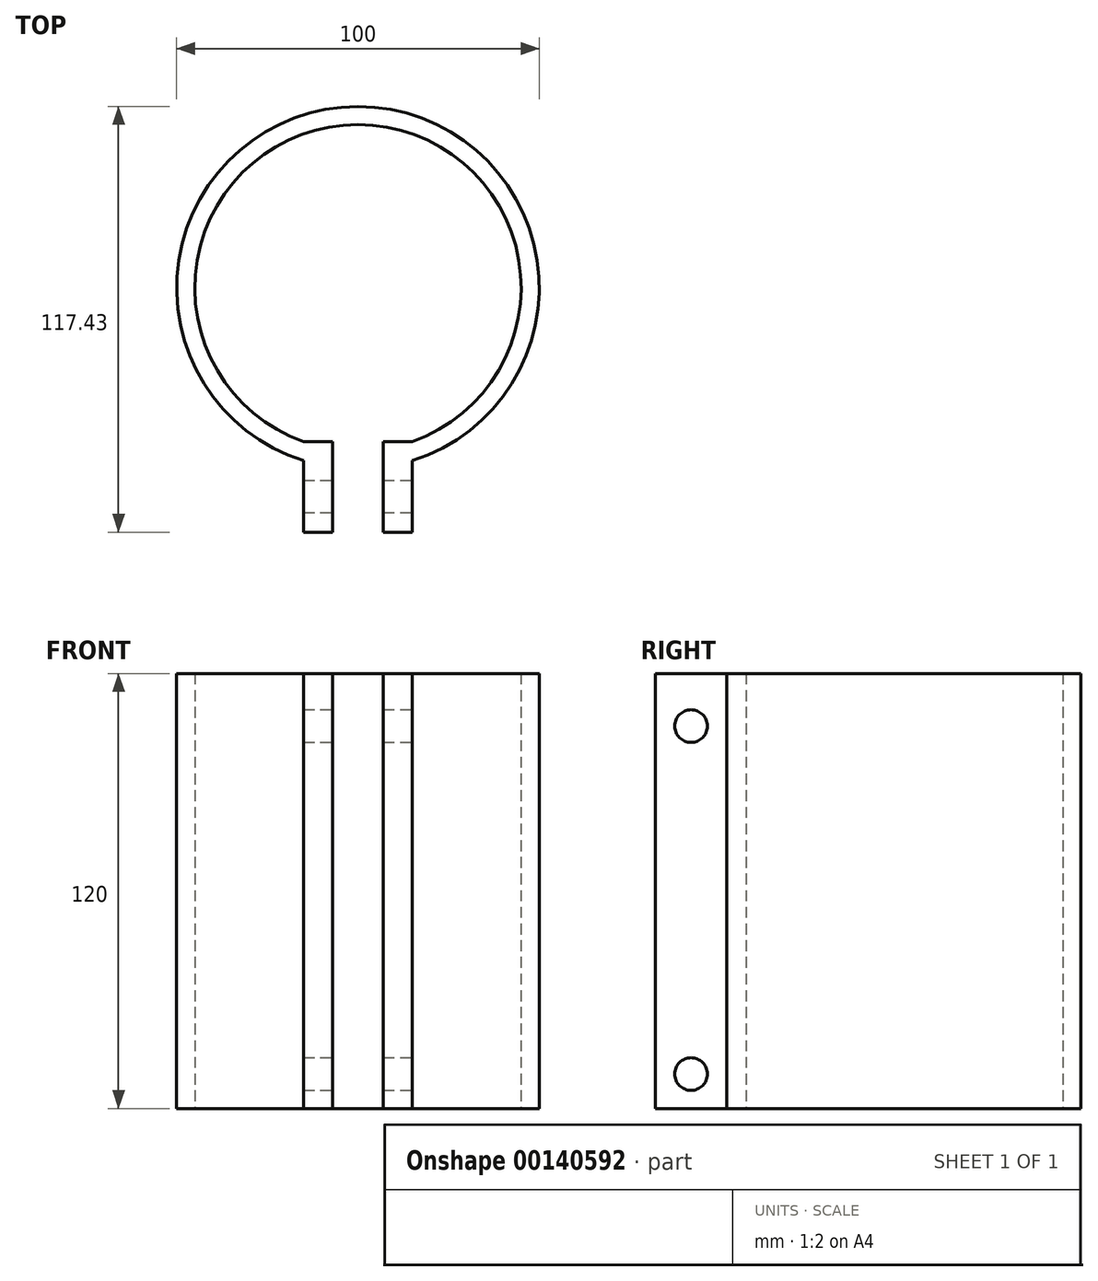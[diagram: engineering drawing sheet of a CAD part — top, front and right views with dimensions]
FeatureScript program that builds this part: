
annotation { "Feature Type Name" : "Feature", "Feature Type Description" : "" }
export const myFeature = defineFeature(function(context is Context, id is Id, definition is map)
    precondition{}
    {
        {
            var Q0;
            Q0=qCreatedBy(makeId("Top.planeOp"),FACE);
            var sketch = newSketch(context, id + "F0", { "sketchPlane" : qUnion([Q0])});
            skLineSegment(sketch, "E0", {"start": v(0, 56.78) * mm, "end": v(0, -71.57) * mm, "construction": true});
            skLineSegment(sketch, "E1", {"start": v(-72.55, 0) * mm, "end": v(74.1, 0) * mm, "construction": true});
            skPoint(sketch, "E2.middle", {"position": v(0, -50) * mm});
            skArc(sketch, "E3", {"start": v(15, -42.43) * mm, "mid": v(0, 45) * mm, "end": v(-15, -42.43) * mm});
            skArc(sketch, "E4", {"start": v(15, -47.7) * mm, "mid": v(0, 50) * mm, "end": v(-15, -47.7) * mm});
            skLineSegment(sketch, "E5.bottom", {"start": v(15, -42.43) * mm, "end": v(7, -42.43) * mm});
            skLineSegment(sketch, "E5.top", {"start": v(15, -67.43) * mm, "end": v(7, -67.43) * mm});
            skLineSegment(sketch, "E5.left", {"start": v(15, -42.43) * mm, "end": v(15, -67.43) * mm});
            skLineSegment(sketch, "E5.right", {"start": v(7, -42.43) * mm, "end": v(7, -67.43) * mm});
            skLineSegment(sketch, "E6.MirrorCS", {"start": v(-15, -42.43) * mm, "end": v(-7, -42.43) * mm});
            skLineSegment(sketch, "E7.MirrorCS", {"start": v(-7, -42.43) * mm, "end": v(-7, -67.43) * mm});
            skLineSegment(sketch, "E8.MirrorCS", {"start": v(-15, -42.43) * mm, "end": v(-15, -67.43) * mm});
            skLineSegment(sketch, "E9.MirrorCS", {"start": v(-15, -67.43) * mm, "end": v(-7, -67.43) * mm});
            skLineSegment(sketch, "E10", {"start": v(50, 0) * mm, "end": v(50, 78) * mm});
            skLineSegment(sketch, "E11", {"start": v(-50, 0) * mm, "end": v(-50, 78) * mm});
            skLineSegment(sketch, "E12", {"start": v(-48, 80) * mm, "end": v(48, 80) * mm});
            skPoint(sketch, "E13.visualSharp", {"position": v(-50, 80) * mm});
            skArc(sketch, "E13.filletArc", {"start": v(-48, 80) * mm, "mid": v(-49.41, 79.41) * mm, "end": v(-50, 78) * mm});
            skPoint(sketch, "E14.visualSharp", {"position": v(50, 80) * mm});
            skArc(sketch, "E14.filletArc", {"start": v(50, 78) * mm, "mid": v(49.41, 79.41) * mm, "end": v(48, 80) * mm});
            skArc(sketch, "E15.0", {"start": v(40, 44.72) * mm, "mid": v(0, 60) * mm, "end": v(-40, 44.72) * mm});
            skLineSegment(sketch, "E16.0", {"start": v(-40, 75) * mm, "end": v(40, 75) * mm});
            skLineSegment(sketch, "E17.trimOffspring", {"start": v(-40, 44.72) * mm, "end": v(-40, 75) * mm});
            skLineSegment(sketch, "E18.trimOffspring", {"start": v(40, 44.72) * mm, "end": v(40, 75) * mm});
            skLineSegment(sketch, "E19", {"start": v(-40, 75) * mm, "end": v(-50, 75) * mm});
            skLineSegment(sketch, "E20", {"start": v(40, 75) * mm, "end": v(50, 75) * mm});
            skSolve(sketch);
        }
        {
            var Q0;
            {var subQ7=sQuery(id+"F0.wireOp",EDGE,"E3");Q0=makeQuery(id+"F0.imprint","IMPRINT",FACE,{"disambiguationData":[TD([[makeQuery(id+"F0.imprint","IMPRINT",EDGE,{"derivedFrom":subQ7}),-1.0]])]});}
            var Q1;
            {var subQ3=sQuery(id+"F0.wireOp",EDGE,"E5.bottom");Q1=makeQuery(id+"F0.imprint","IMPRINT",FACE,{"disambiguationData":[TD([[makeQuery(id+"F0.imprint","IMPRINT",EDGE,{"derivedFrom":subQ3}),1.0]])]});}
            var Q2;
            {var subQ3=sQuery(id+"F0.wireOp",EDGE,"E6.MirrorCS");Q2=makeQuery(id+"F0.imprint","IMPRINT",FACE,{"disambiguationData":[TD([[makeQuery(id+"F0.imprint","IMPRINT",EDGE,{"derivedFrom":subQ3}),-1.0]])]});}
            extrude(context, id + "F1", {"entities" : qUnion([Q0, Q1, Q2]), "depth" : 120 * mm});
        }
        {
            var Q0;
            Q0=makeQuery(id+"F1.opExtrude","SWEPT_FACE",FACE,{"disambiguationData":[OSD([sQuery(id+"F0.wireOp",EDGE,"E5.left")])]});
            var sketch = newSketch(context, id + "F2", { "sketchPlane" : qUnion([Q0])});
            skCircle(sketch, "E21", {"center": v(-57.56, 105.5) * mm, "radius": 4.5 * mm});
            skPoint(sketch, "E21.centerSnap0", {"position": v(-57.56, 120) * mm});
            skCircle(sketch, "E22", {"center": v(-57.56, 9.5) * mm, "radius": 4.5 * mm});
            skPoint(sketch, "E22.centerSnap0", {"position": v(-57.56, 0) * mm});
            skSolve(sketch);
        }
        {
            var Q0;
            Q0 = qSketchRegion(id + "F2", true);
            extrude(context, id + "F3", {"entities" : qUnion([Q0]), "operationType" : NewBodyOperationType.REMOVE, "oppositeDirection" : true, "depth" : 50 * mm});
        }
    });
